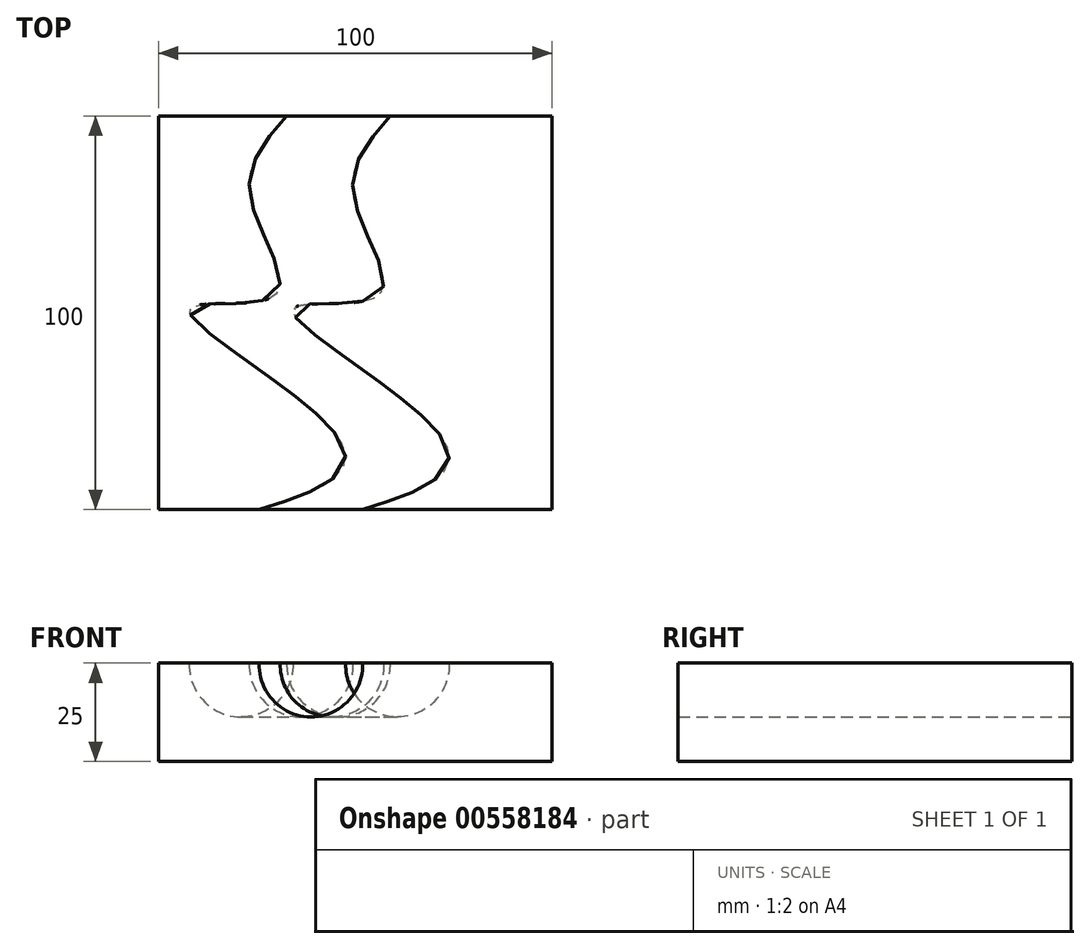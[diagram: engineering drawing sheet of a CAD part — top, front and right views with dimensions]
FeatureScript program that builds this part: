
annotation { "Feature Type Name" : "Feature", "Feature Type Description" : "" }
export const myFeature = defineFeature(function(context is Context, id is Id, definition is map)
    precondition{}
    {
        {
            var Q0;
            Q0=qCreatedBy(makeId("Top.planeOp"),FACE);
            var sketch = newSketch(context, id + "F0", { "sketchPlane" : qUnion([Q0])});
            skLineSegment(sketch, "E0.bottom", {"start": v(0, 0) * mm, "end": v(100, 0) * mm});
            skLineSegment(sketch, "E0.top", {"start": v(0, -100) * mm, "end": v(100, -100) * mm});
            skLineSegment(sketch, "E0.left", {"start": v(0, 0) * mm, "end": v(0, -100) * mm});
            skLineSegment(sketch, "E0.right", {"start": v(100, 0) * mm, "end": v(100, -100) * mm});
            skSolve(sketch);
        }
        {
            var Q0;
            Q0 = qSketchRegion(id + "F0", true);
            extrude(context, id + "F1", {"entities" : qUnion([Q0]), "oppositeDirection" : true, "depth" : 50 * mm, "offsetDistance" : 25 * mm});
        }
        {
            var Q0;
            Q0=makeQuery(id+"F1.opExtrude","CAP_FACE",FACE,{"disambiguationData":[OSD([sQuery(id+"F0.wireOp",EDGE,"E0.bottom"),sQuery(id+"F0.wireOp",EDGE,"E0.top"),sQuery(id+"F0.wireOp",EDGE,"E0.left"),sQuery(id+"F0.wireOp",EDGE,"E0.right")])],"isStart":true});
            cPlane(context, id + "F2", {"entities" : qUnion([Q0]), "cplaneType" : CPlaneType.OFFSET, "offset" : 25 * mm, "oppositeDirection" : true, "width" : 150 * mm, "height" : 150 * mm});
        }
        {
            var Q0;
            Q0=qCreatedBy(id+"F2.planeOp",FACE);
            var sketch = newSketch(context, id + "F3", { "sketchPlane" : qUnion([Q0])});
            skFitSpline(sketch, "E1", {"points": [v(37.2, -100.65) * mm, v(60.73, -84) * mm, v(21.6, -49.25) * mm, v(43.37, -45.5) * mm, v(37.05, -20.6) * mm, v(46.33, 0) * mm], "startDerivative": vector(205.05, 62.93) * mm, "endDerivative": vector(92.29, 103.64) * mm});
            skSolve(sketch);
        }
        {
            var Q0;
            Q0=makeQuery(id+"F1.opExtrude","SWEPT_FACE",FACE,{"disambiguationData":[OSD([sQuery(id+"F0.wireOp",EDGE,"E0.top")])]});
            var sketch = newSketch(context, id + "F4", { "sketchPlane" : qUnion([Q0])});
            skCircle(sketch, "E2", {"center": v(38.7, -25.5) * mm, "radius": 13.15 * mm});
            skSolve(sketch);
        }
        {
            var Q0;
            Q0=makeQuery(id+"F4.imprint","IMPRINT",FACE,{"disambiguationData":[TD([[makeQuery(id+"F4.imprint","IMPRINT",EDGE,{"derivedFrom":sQuery(id+"F4.wireOp",EDGE,"E2")}),1.0]])]});
            var Q1;
            Q1=sQuery(id+"F3.wireOp",EDGE,"E1");
            sweep(context, id + "F5", {"operationType" : NewBodyOperationType.REMOVE, "profiles" : qUnion([Q0]), "path" : qUnion([Q1]), "keepProfileOrientation" : true});
        }
        {
            var Q0;
            Q0=makeQuery(id+"F1.opExtrude","CAP_FACE",FACE,{"disambiguationData":[OSD([sQuery(id+"F0.wireOp",EDGE,"E0.bottom"),sQuery(id+"F0.wireOp",EDGE,"E0.top"),sQuery(id+"F0.wireOp",EDGE,"E0.left"),sQuery(id+"F0.wireOp",EDGE,"E0.right")])],"isStart":true});
            var sketch = newSketch(context, id + "F6", { "sketchPlane" : qUnion([Q0])});
            skLineSegment(sketch, "E3.bottom", {"start": v(0, 0) * mm, "end": v(100, 0) * mm});
            skLineSegment(sketch, "E3.top", {"start": v(0, -100) * mm, "end": v(100, -100) * mm});
            skLineSegment(sketch, "E3.left", {"start": v(0, 0) * mm, "end": v(0, -100) * mm});
            skLineSegment(sketch, "E3.right", {"start": v(100, 0) * mm, "end": v(100, -100) * mm});
            skSolve(sketch);
        }
        {
            var Q0;
            Q0 = qSketchRegion(id + "F6", true);
            extrude(context, id + "F7", {"entities" : qUnion([Q0]), "operationType" : NewBodyOperationType.REMOVE, "oppositeDirection" : true, "depth" : 25 * mm, "offsetDistance" : 25 * mm});
        }
    });
